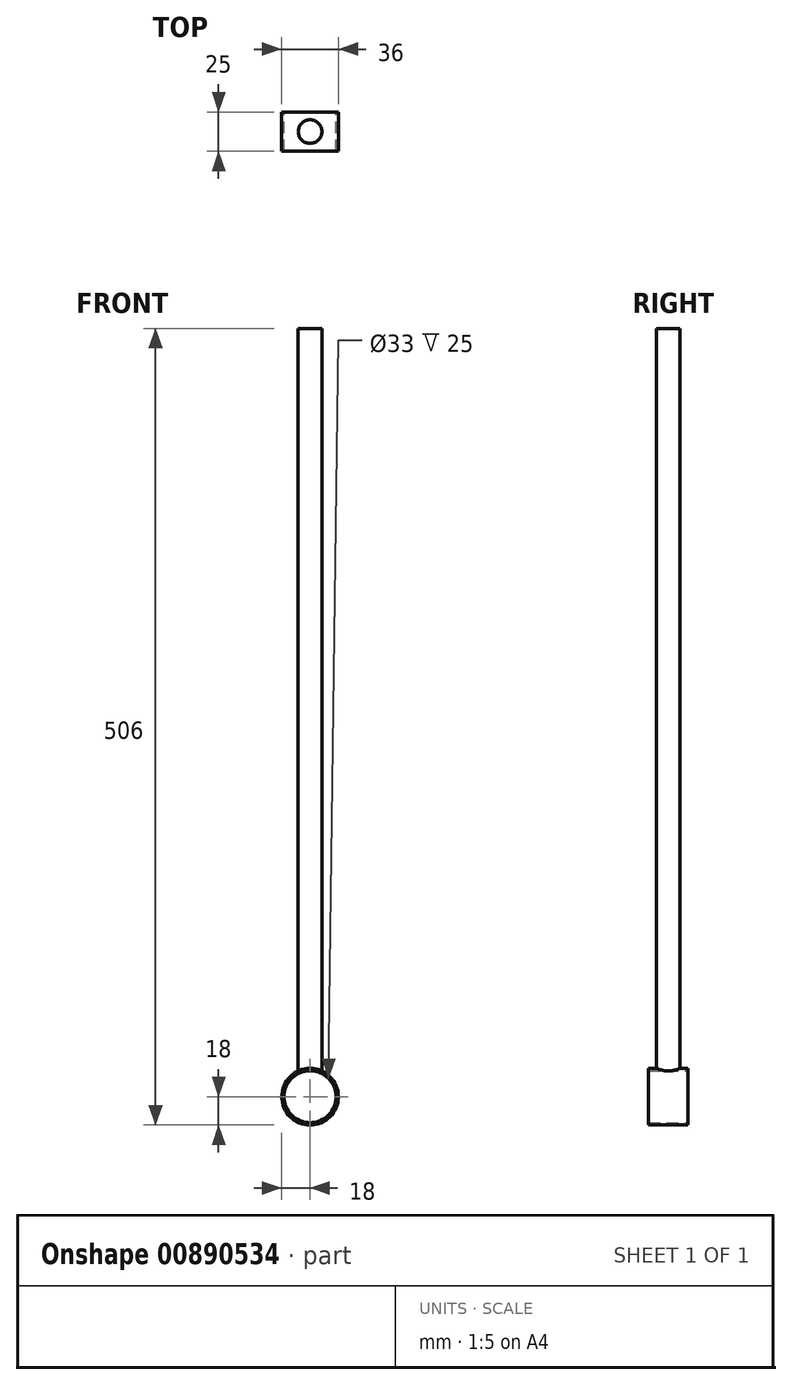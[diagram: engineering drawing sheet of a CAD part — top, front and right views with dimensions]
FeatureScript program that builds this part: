
annotation { "Feature Type Name" : "Feature", "Feature Type Description" : "" }
export const myFeature = defineFeature(function(context is Context, id is Id, definition is map)
    precondition{}
    {
        {
            var Q0;
            Q0=qCreatedBy(makeId("Front.planeOp"),FACE);
            var sketch = newSketch(context, id + "F0", { "sketchPlane" : qUnion([Q0])});
            skCircle(sketch, "E0", {"center": v(0, 0) * mm, "radius": 18 * mm});
            skCircle(sketch, "E1", {"center": v(0, 0) * mm, "radius": 16.5 * mm});
            skSolve(sketch);
        }
        {
            var Q0;
            Q0 = qSketchRegion(id + "F0", true);
            extrude(context, id + "F1", {"entities" : qUnion([Q0]), "depth" : 25 * mm, "offsetDistance" : 25 * mm});
        }
        {
            var Q0;
            Q0=qCreatedBy(makeId("Top.planeOp"),FACE);
            var sketch = newSketch(context, id + "F2", { "sketchPlane" : qUnion([Q0])});
            skCircle(sketch, "E2", {"center": v(0, -12.5) * mm, "radius": 7.5 * mm});
            skSolve(sketch);
        }
        {
            var Q0;
            Q0 = qSketchRegion(id + "F2", true);
            extrude(context, id + "F3", {"entities" : qUnion([Q0]), "operationType" : NewBodyOperationType.ADD, "depth" : 488 * mm, "offsetDistance" : 25 * mm});
        }
        {
            var Q0;
            Q0=makeQuery(id+"F3.opExtrude","CAP_FACE",FACE,{"disambiguationData":[OSD([sQuery(id+"F2.wireOp",EDGE,"E2")])],"isStart":true});
            var Q1;
            Q1=makeQuery(id+"F1.opExtrude","SWEPT_FACE",FACE,{"disambiguationData":[OSD([sQuery(id+"F0.wireOp",EDGE,"E1")])]});
            extrude(context, id + "F4", {"entities" : qUnion([Q0]), "operationType" : NewBodyOperationType.REMOVE, "endBound" : BoundingType.UP_TO_SURFACE, "oppositeDirection" : true, "depth" : 25 * mm, "endBoundEntityFace" : qUnion([Q1]), "offsetDistance" : 25 * mm});
        }
    });
